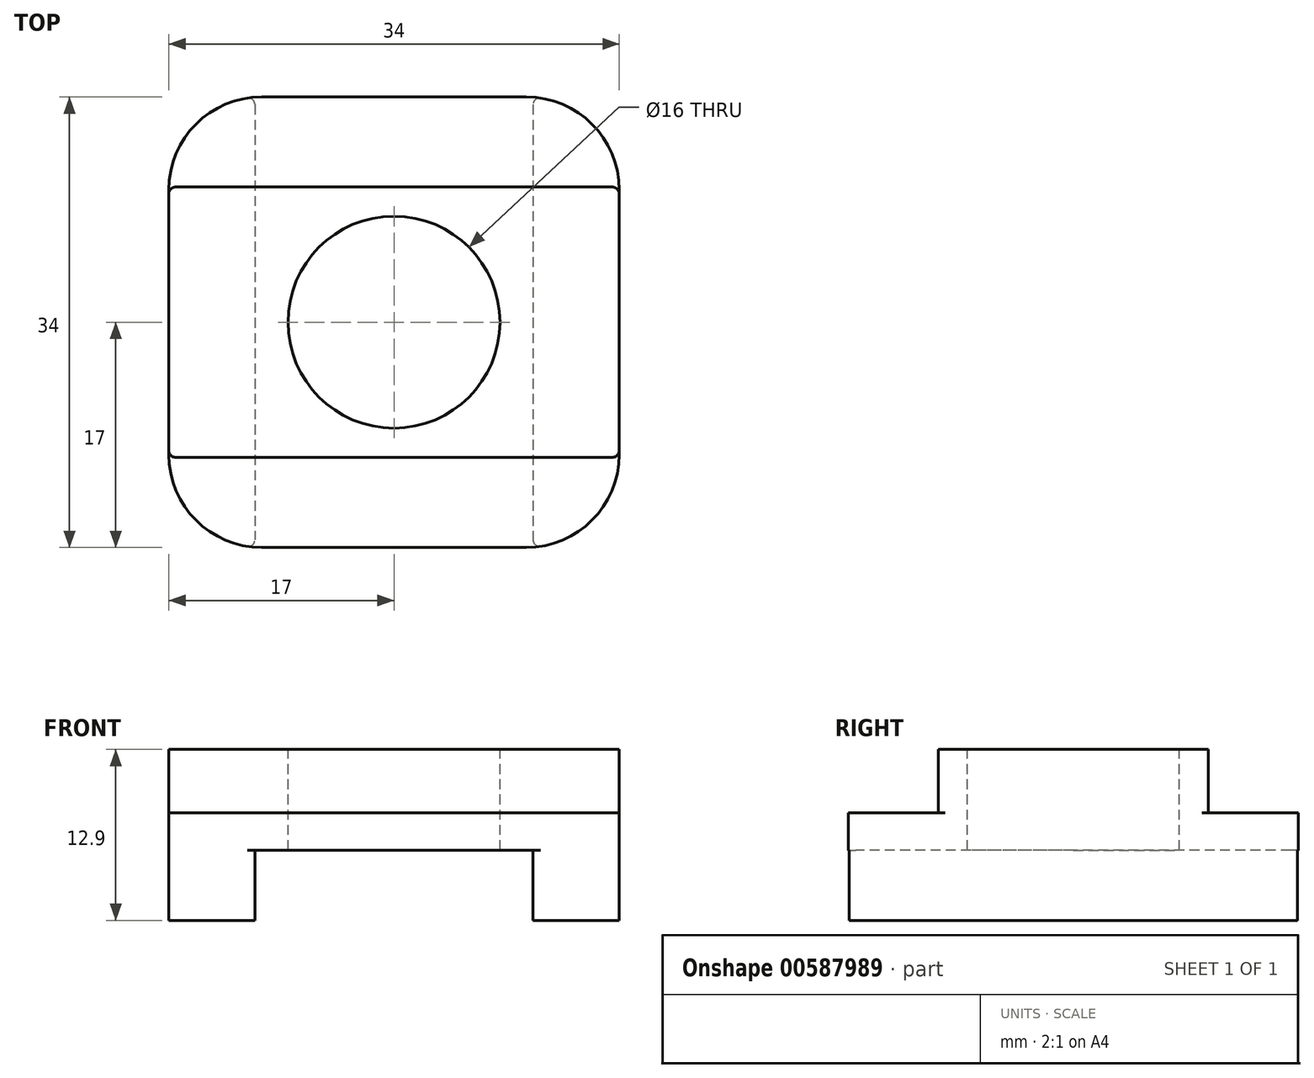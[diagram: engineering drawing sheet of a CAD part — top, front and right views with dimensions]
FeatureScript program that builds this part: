
annotation { "Feature Type Name" : "Feature", "Feature Type Description" : "" }
export const myFeature = defineFeature(function(context is Context, id is Id, definition is map)
    precondition{}
    {
        {
            var Q0;
            Q0=qCreatedBy(makeId("Top.planeOp"),FACE);
            var sketch = newSketch(context, id + "F0", { "sketchPlane" : qUnion([Q0])});
            skLineSegment(sketch, "E0.bottom", {"start": v(-17, 17) * mm, "end": v(17, 17) * mm});
            skLineSegment(sketch, "E0.top", {"start": v(-17, -17) * mm, "end": v(17, -17) * mm});
            skLineSegment(sketch, "E0.left", {"start": v(-17, 17) * mm, "end": v(-17, -17) * mm});
            skLineSegment(sketch, "E0.right", {"start": v(17, 17) * mm, "end": v(17, -17) * mm});
            skPoint(sketch, "E1", {"position": v(0, 17) * mm});
            skPoint(sketch, "E2", {"position": v(17, 0) * mm});
            skSolve(sketch);
        }
        {
            var Q0;
            Q0 = qSketchRegion(id + "F0", true);
            extrude(context, id + "F1", {"entities" : qUnion([Q0]), "depth" : 12.9 * mm, "offsetDistance" : 25 * mm});
        }
        {
            var Q0;
            Q0=makeQuery(id+"F1.opExtrude","SWEPT_FACE",FACE,{"disambiguationData":[OSD([sQuery(id+"F0.wireOp",EDGE,"E0.top")])]});
            var sketch = newSketch(context, id + "F2", { "sketchPlane" : qUnion([Q0])});
            skLineSegment(sketch, "E3.bottom", {"start": v(-10.5, 0) * mm, "end": v(10.5, 0) * mm});
            skLineSegment(sketch, "E3.top", {"start": v(-10.5, 5.3) * mm, "end": v(10.5, 5.3) * mm});
            skLineSegment(sketch, "E3.left", {"start": v(-10.5, 0) * mm, "end": v(-10.5, 5.3) * mm});
            skLineSegment(sketch, "E3.right", {"start": v(10.5, 0) * mm, "end": v(10.5, 5.3) * mm});
            skPoint(sketch, "E4", {"position": v(0, 0) * mm});
            skSolve(sketch);
        }
        {
            var Q0;
            Q0 = qSketchRegion(id + "F2", true);
            extrude(context, id + "F3", {"entities" : qUnion([Q0]), "operationType" : NewBodyOperationType.REMOVE, "endBound" : BoundingType.THROUGH_ALL, "oppositeDirection" : true, "depth" : 25 * mm, "offsetDistance" : 25 * mm});
        }
        {
            var Q0;
            Q0=makeQuery(id+"F1.opExtrude","SWEPT_FACE",FACE,{"disambiguationData":[OSD([sQuery(id+"F0.wireOp",EDGE,"E0.right")])]});
            var sketch = newSketch(context, id + "F4", { "sketchPlane" : qUnion([Q0])});
            skLineSegment(sketch, "E5.bottom", {"start": v(-17, 12.9) * mm, "end": v(-10.2, 12.9) * mm});
            skLineSegment(sketch, "E5.top", {"start": v(-17, 8.1) * mm, "end": v(-10.2, 8.1) * mm});
            skLineSegment(sketch, "E5.left", {"start": v(-17, 12.9) * mm, "end": v(-17, 8.1) * mm});
            skLineSegment(sketch, "E5.right", {"start": v(-10.2, 12.9) * mm, "end": v(-10.2, 8.1) * mm});
            skLineSegment(sketch, "E6.MirrorCS", {"start": v(17, 8.1) * mm, "end": v(10.2, 8.1) * mm});
            skLineSegment(sketch, "E7.MirrorCS", {"start": v(10.2, 12.9) * mm, "end": v(10.2, 8.1) * mm});
            skLineSegment(sketch, "E8.MirrorCS", {"start": v(17, 12.9) * mm, "end": v(17, 8.1) * mm});
            skLineSegment(sketch, "E9.MirrorCS", {"start": v(17, 12.9) * mm, "end": v(10.2, 12.9) * mm});
            skSolve(sketch);
        }
        {
            var Q0;
            Q0 = qSketchRegion(id + "F4", true);
            extrude(context, id + "F5", {"entities" : qUnion([Q0]), "operationType" : NewBodyOperationType.REMOVE, "endBound" : BoundingType.THROUGH_ALL, "oppositeDirection" : true, "depth" : 25 * mm, "offsetDistance" : 25 * mm});
        }
        {
            var Q0;
            Q0=makeQuery(id+"F1.opExtrude","CAP_FACE",FACE,{"disambiguationData":[OSD([sQuery(id+"F0.wireOp",EDGE,"E0.bottom"),sQuery(id+"F0.wireOp",EDGE,"E0.top"),sQuery(id+"F0.wireOp",EDGE,"E0.left"),sQuery(id+"F0.wireOp",EDGE,"E0.right")])],"isStart":false});
            var sketch = newSketch(context, id + "F6", { "sketchPlane" : qUnion([Q0])});
            skCircle(sketch, "E10", {"center": v(0, 0) * mm, "radius": 8 * mm});
            skSolve(sketch);
        }
        {
            var Q0;
            Q0 = qSketchRegion(id + "F6", true);
            extrude(context, id + "F7", {"entities" : qUnion([Q0]), "operationType" : NewBodyOperationType.REMOVE, "endBound" : BoundingType.THROUGH_ALL, "oppositeDirection" : true, "depth" : 25 * mm, "offsetDistance" : 25 * mm});
        }
        {
            var Q0;
            Q0=makeQuery(id+"F1.opExtrude","SWEPT_EDGE",EDGE,{"disambiguationData":[OSD([sQuery(id+"F0.wireOp",EDGE,"E0.top"),sQuery(id+"F0.wireOp",EDGE,"E0.right")])]});
            var Q1;
            Q1=makeQuery(id+"F1.opExtrude","SWEPT_EDGE",EDGE,{"disambiguationData":[OSD([sQuery(id+"F0.wireOp",EDGE,"E0.bottom"),sQuery(id+"F0.wireOp",EDGE,"E0.right")])]});
            var Q2;
            Q2=makeQuery(id+"F1.opExtrude","SWEPT_EDGE",EDGE,{"disambiguationData":[OSD([sQuery(id+"F0.wireOp",EDGE,"E0.top"),sQuery(id+"F0.wireOp",EDGE,"E0.left")])]});
            var Q3;
            Q3=makeQuery(id+"F1.opExtrude","SWEPT_EDGE",EDGE,{"disambiguationData":[OSD([sQuery(id+"F0.wireOp",EDGE,"E0.bottom"),sQuery(id+"F0.wireOp",EDGE,"E0.left")])]});
            fillet(context, id + "F8", {"entities" : qUnion([Q0, Q1, Q2, Q3]), "radius" : 7 * mm, "tangentPropagation" : true, "allowEdgeOverflow" : false});
        }
        {
            var Q0;
            Q0=makeQuery(id+"F8.opFillet","BLEND_EDGE",EDGE,{"blendedFrom":[makeQuery(id+"F1.opExtrude","SWEPT_EDGE",EDGE,{"disambiguationData":[OSD([sQuery(id+"F0.wireOp",EDGE,"E0.top"),sQuery(id+"F0.wireOp",EDGE,"E0.right")])]}),makeQuery(id+"F5.boolean.opBoolean","COPY",FACE,{"derivedFrom":makeQuery(id+"F5.opExtrude","SWEPT_FACE",FACE,{"disambiguationData":[OSD([sQuery(id+"F4.wireOp",EDGE,"E5.right")])]})})],"blendedInto":[makeQuery(id+"F5.boolean.opBoolean","COPY",FACE,{"derivedFrom":makeQuery(id+"F5.opExtrude","SWEPT_FACE",FACE,{"disambiguationData":[OSD([sQuery(id+"F4.wireOp",EDGE,"E5.right")])]})})]});
            var Q1;
            Q1=makeQuery(id+"F8.opFillet","BLEND_EDGE",EDGE,{"blendedFrom":[makeQuery(id+"F1.opExtrude","SWEPT_EDGE",EDGE,{"disambiguationData":[OSD([sQuery(id+"F0.wireOp",EDGE,"E0.bottom"),sQuery(id+"F0.wireOp",EDGE,"E0.right")])]}),makeQuery(id+"F5.boolean.opBoolean","COPY",FACE,{"derivedFrom":makeQuery(id+"F5.opExtrude","SWEPT_FACE",FACE,{"disambiguationData":[OSD([sQuery(id+"F4.wireOp",EDGE,"E7.MirrorCS")])]})})],"blendedInto":[makeQuery(id+"F5.boolean.opBoolean","COPY",FACE,{"derivedFrom":makeQuery(id+"F5.opExtrude","SWEPT_FACE",FACE,{"disambiguationData":[OSD([sQuery(id+"F4.wireOp",EDGE,"E7.MirrorCS")])]})})]});
            var Q2;
            Q2=makeQuery(id+"F8.opFillet","BLEND_EDGE",EDGE,{"blendedFrom":[makeQuery(id+"F1.opExtrude","SWEPT_EDGE",EDGE,{"disambiguationData":[OSD([sQuery(id+"F0.wireOp",EDGE,"E0.top"),sQuery(id+"F0.wireOp",EDGE,"E0.right")])]}),makeQuery(id+"F3.boolean.opBoolean","COPY",FACE,{"derivedFrom":makeQuery(id+"F3.opExtrude","SWEPT_FACE",FACE,{"disambiguationData":[OSD([sQuery(id+"F2.wireOp",EDGE,"E3.right")])]})})],"blendedInto":[makeQuery(id+"F3.boolean.opBoolean","COPY",FACE,{"derivedFrom":makeQuery(id+"F3.opExtrude","SWEPT_FACE",FACE,{"disambiguationData":[OSD([sQuery(id+"F2.wireOp",EDGE,"E3.right")])]})})]});
            var Q3;
            Q3=makeQuery(id+"F8.opFillet","BLEND_EDGE",EDGE,{"blendedFrom":[makeQuery(id+"F1.opExtrude","SWEPT_EDGE",EDGE,{"disambiguationData":[OSD([sQuery(id+"F0.wireOp",EDGE,"E0.top"),sQuery(id+"F0.wireOp",EDGE,"E0.left")])]}),makeQuery(id+"F3.boolean.opBoolean","COPY",FACE,{"derivedFrom":makeQuery(id+"F3.opExtrude","SWEPT_FACE",FACE,{"disambiguationData":[OSD([sQuery(id+"F2.wireOp",EDGE,"E3.left")])]})})],"blendedInto":[makeQuery(id+"F3.boolean.opBoolean","COPY",FACE,{"derivedFrom":makeQuery(id+"F3.opExtrude","SWEPT_FACE",FACE,{"disambiguationData":[OSD([sQuery(id+"F2.wireOp",EDGE,"E3.left")])]})})]});
            var Q4;
            Q4=makeQuery(id+"F8.opFillet","BLEND_EDGE",EDGE,{"blendedFrom":[makeQuery(id+"F1.opExtrude","SWEPT_EDGE",EDGE,{"disambiguationData":[OSD([sQuery(id+"F0.wireOp",EDGE,"E0.bottom"),sQuery(id+"F0.wireOp",EDGE,"E0.left")])]}),makeQuery(id+"F5.boolean.opBoolean","COPY",FACE,{"derivedFrom":makeQuery(id+"F5.opExtrude","SWEPT_FACE",FACE,{"disambiguationData":[OSD([sQuery(id+"F4.wireOp",EDGE,"E7.MirrorCS")])]})})],"blendedInto":[makeQuery(id+"F5.boolean.opBoolean","COPY",FACE,{"derivedFrom":makeQuery(id+"F5.opExtrude","SWEPT_FACE",FACE,{"disambiguationData":[OSD([sQuery(id+"F4.wireOp",EDGE,"E7.MirrorCS")])]})})]});
            var Q5;
            Q5=makeQuery(id+"F8.opFillet","BLEND_EDGE",EDGE,{"blendedFrom":[makeQuery(id+"F1.opExtrude","SWEPT_EDGE",EDGE,{"disambiguationData":[OSD([sQuery(id+"F0.wireOp",EDGE,"E0.bottom"),sQuery(id+"F0.wireOp",EDGE,"E0.left")])]}),makeQuery(id+"F3.boolean.opBoolean","COPY",FACE,{"derivedFrom":makeQuery(id+"F3.opExtrude","SWEPT_FACE",FACE,{"disambiguationData":[OSD([sQuery(id+"F2.wireOp",EDGE,"E3.left")])]})})],"blendedInto":[makeQuery(id+"F3.boolean.opBoolean","COPY",FACE,{"derivedFrom":makeQuery(id+"F3.opExtrude","SWEPT_FACE",FACE,{"disambiguationData":[OSD([sQuery(id+"F2.wireOp",EDGE,"E3.left")])]})})]});
            var Q6;
            Q6=makeQuery(id+"F8.opFillet","BLEND_EDGE",EDGE,{"blendedFrom":[makeQuery(id+"F1.opExtrude","SWEPT_EDGE",EDGE,{"disambiguationData":[OSD([sQuery(id+"F0.wireOp",EDGE,"E0.bottom"),sQuery(id+"F0.wireOp",EDGE,"E0.right")])]}),makeQuery(id+"F3.boolean.opBoolean","COPY",FACE,{"derivedFrom":makeQuery(id+"F3.opExtrude","SWEPT_FACE",FACE,{"disambiguationData":[OSD([sQuery(id+"F2.wireOp",EDGE,"E3.right")])]})})],"blendedInto":[makeQuery(id+"F3.boolean.opBoolean","COPY",FACE,{"derivedFrom":makeQuery(id+"F3.opExtrude","SWEPT_FACE",FACE,{"disambiguationData":[OSD([sQuery(id+"F2.wireOp",EDGE,"E3.right")])]})})]});
            var Q7;
            Q7=makeQuery(id+"F8.opFillet","BLEND_EDGE",EDGE,{"blendedFrom":[makeQuery(id+"F1.opExtrude","SWEPT_EDGE",EDGE,{"disambiguationData":[OSD([sQuery(id+"F0.wireOp",EDGE,"E0.top"),sQuery(id+"F0.wireOp",EDGE,"E0.left")])]}),makeQuery(id+"F5.boolean.opBoolean","COPY",FACE,{"derivedFrom":makeQuery(id+"F5.opExtrude","SWEPT_FACE",FACE,{"disambiguationData":[OSD([sQuery(id+"F4.wireOp",EDGE,"E5.right")])]})})],"blendedInto":[makeQuery(id+"F5.boolean.opBoolean","COPY",FACE,{"derivedFrom":makeQuery(id+"F5.opExtrude","SWEPT_FACE",FACE,{"disambiguationData":[OSD([sQuery(id+"F4.wireOp",EDGE,"E5.right")])]})})]});
            fillet(context, id + "F9", {"entities" : qUnion([Q0, Q1, Q2, Q3, Q4, Q5, Q6, Q7]), "radius" : 0.5 * mm, "tangentPropagation" : true, "allowEdgeOverflow" : false});
        }
    });
